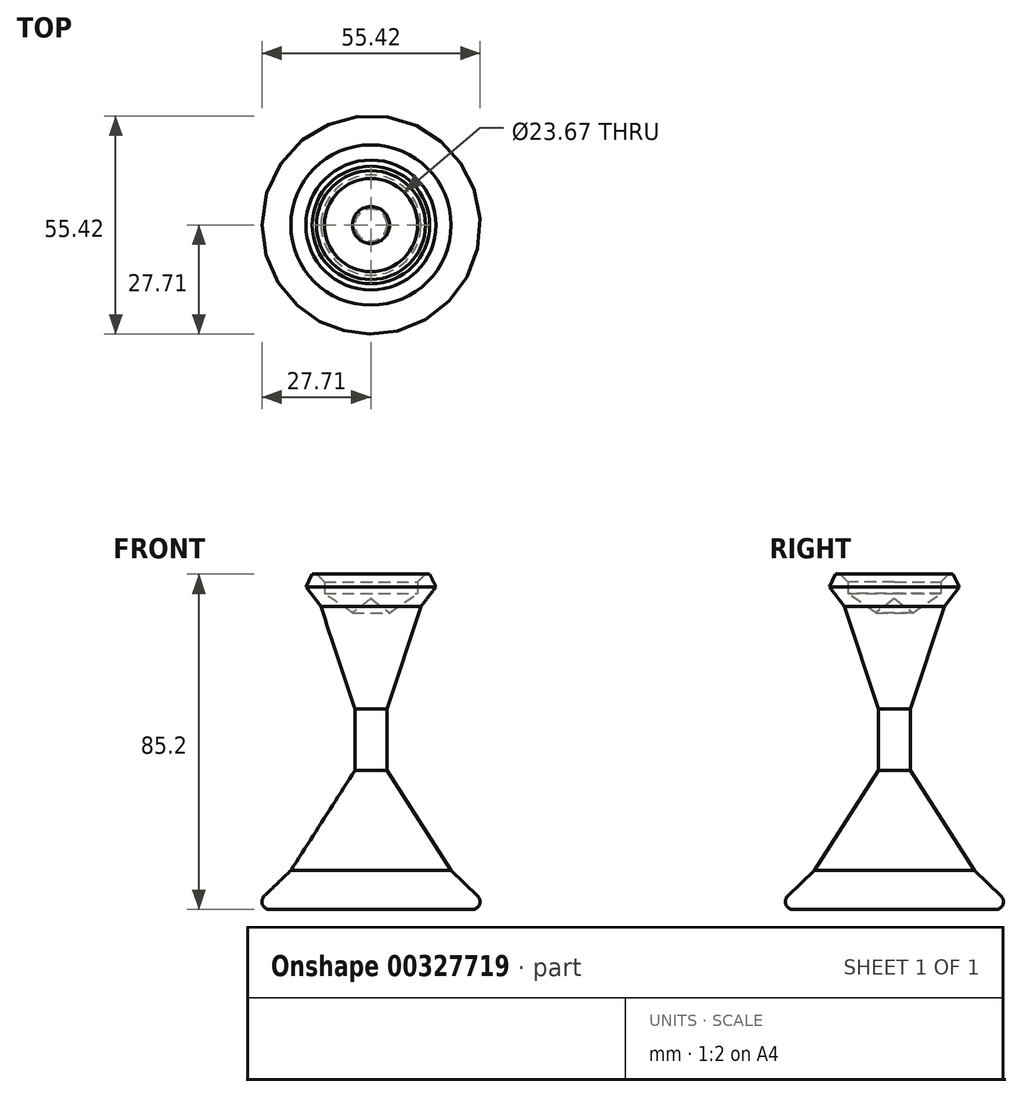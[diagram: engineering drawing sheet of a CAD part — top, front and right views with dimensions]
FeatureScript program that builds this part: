
annotation { "Feature Type Name" : "Feature", "Feature Type Description" : "" }
export const myFeature = defineFeature(function(context is Context, id is Id, definition is map)
    precondition{}
    {
        {
            var Q0;
            Q0=qCreatedBy(makeId("Front.planeOp"),FACE);
            var sketch = newSketch(context, id + "F0", { "sketchPlane" : qUnion([Q0])});
            skLineSegment(sketch, "E0.MirrorCS", {"start": v(20.36, 9.92) * mm, "end": v(4.07, 35.35) * mm});
            skLineSegment(sketch, "E1.MirrorCS", {"start": v(30.68, 0) * mm, "end": v(20.36, 9.92) * mm});
            skLineSegment(sketch, "E2.MirrorCS", {"start": v(12.72, 77.02) * mm, "end": v(4.07, 50.9) * mm});
            skLineSegment(sketch, "E3.MirrorCS", {"start": v(18.97, 85.2) * mm, "end": v(12.72, 77.02) * mm});
            skLineSegment(sketch, "E4", {"start": v(-30.68, 0) * mm, "end": v(30.68, 0) * mm});
            skLineSegment(sketch, "E5", {"start": v(4.07, 50.9) * mm, "end": v(4.07, 35.35) * mm});
            skLineSegment(sketch, "E6", {"start": v(0, 79) * mm, "end": v(0, 0) * mm});
            skLineSegment(sketch, "E7", {"start": v(0, 0) * mm, "end": v(0, 79) * mm});
            skLineSegment(sketch, "E8", {"start": v(4.7, 75.41) * mm, "end": v(0, 79) * mm});
            skPoint(sketch, "E9", {"position": v(11.84, 80.3) * mm});
            skLineSegment(sketch, "E10", {"start": v(11.84, 85.2) * mm, "end": v(11.84, 80.3) * mm});
            skLineSegment(sketch, "E11", {"start": v(18.97, 85.2) * mm, "end": v(11.84, 85.2) * mm});
            skLineSegment(sketch, "E12", {"start": v(11.84, 80.3) * mm, "end": v(4.7, 75.41) * mm});
            skLineSegment(sketch, "E13", {"start": v(0, 0) * mm, "end": v(0, 135.43) * mm});
            skLineSegment(sketch, "E14.MirrorCS", {"start": v(-4.7, 75.41) * mm, "end": v(0, 79) * mm});
            skLineSegment(sketch, "E15.MirrorCS", {"start": v(-11.84, 80.3) * mm, "end": v(-4.7, 75.41) * mm});
            skLineSegment(sketch, "E16.MirrorCS", {"start": v(-11.84, 85.2) * mm, "end": v(-11.84, 80.3) * mm});
            skLineSegment(sketch, "E17.MirrorCS", {"start": v(-18.97, 85.2) * mm, "end": v(-11.84, 85.2) * mm});
            skLineSegment(sketch, "E18.MirrorCS", {"start": v(-18.97, 85.2) * mm, "end": v(-12.72, 77.02) * mm});
            skLineSegment(sketch, "E19.MirrorCS", {"start": v(-12.72, 77.02) * mm, "end": v(-4.07, 50.9) * mm});
            skLineSegment(sketch, "E20.MirrorCS", {"start": v(-4.07, 50.9) * mm, "end": v(-4.07, 35.35) * mm});
            skLineSegment(sketch, "E21.MirrorCS", {"start": v(-20.36, 9.92) * mm, "end": v(-4.07, 35.35) * mm});
            skLineSegment(sketch, "E22.MirrorCS", {"start": v(-30.68, 0) * mm, "end": v(-20.36, 9.92) * mm});
            skSolve(sketch);
        }
        {
            var Q0;
            Q0=makeQuery(id+"F0.imprint","IMPRINT",FACE,{"disambiguationData":[TD([[makeQuery(id+"F0.imprint","IMPRINT",EDGE,{"derivedFrom":sQuery(id+"F0.wireOp",EDGE,"E0.MirrorCS")}),1.0]])]});
            var Q1;
            Q1=sQuery(id+"F0.wireOp",EDGE,"E13");
            revolve(context, id + "F1", {"entities" : qUnion([Q0]), "axis" : qUnion([Q1]), "revolveType" : RevolveType.FULL});
        }
        {
            var Q0;
            Q0=makeQuery(id+"F1.opRevolve","SWEPT_EDGE",EDGE,{"disambiguationData":[OSD([sQuery(id+"F0.wireOp",EDGE,"E3.MirrorCS"),sQuery(id+"F0.wireOp",EDGE,"E11")])]});
            var Q1;
            Q1=makeQuery(id+"F1.opRevolve","SWEPT_EDGE",EDGE,{"disambiguationData":[OSD([sQuery(id+"F0.wireOp",EDGE,"E10"),sQuery(id+"F0.wireOp",EDGE,"E11")])]});
            chamfer(context, id + "F2", {"entities" : qUnion([Q0, Q1]), "width" : 2 * mm, "tangentPropagation" : true});
        }
        {
            var Q0;
            Q0=makeQuery(id+"F1.opRevolve","SWEPT_EDGE",EDGE,{"disambiguationData":[OSD([sQuery(id+"F0.wireOp",EDGE,"E1.MirrorCS"),sQuery(id+"F0.wireOp",EDGE,"E4")])]});
            fillet(context, id + "F3", {"entities" : qUnion([Q0]), "radius" : 2 * mm, "tangentPropagation" : true, "allowEdgeOverflow" : false});
        }
    });
